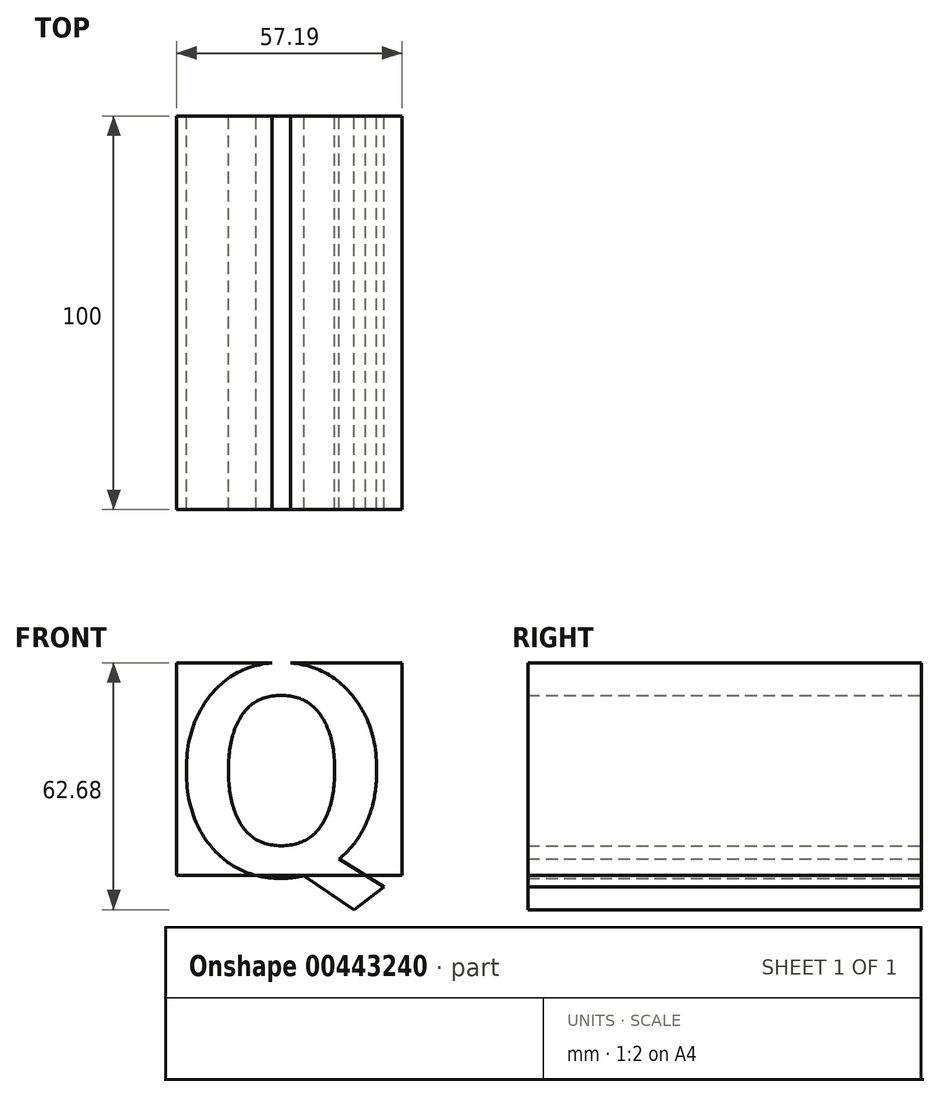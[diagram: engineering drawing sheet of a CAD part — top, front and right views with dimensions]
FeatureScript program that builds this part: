
annotation { "Feature Type Name" : "Feature", "Feature Type Description" : "" }
export const myFeature = defineFeature(function(context is Context, id is Id, definition is map)
    precondition{}
    {
        {
            var Q0;
            Q0=qCreatedBy(makeId("Front.planeOp"),FACE);
            var sketch = newSketch(context, id + "F0", { "sketchPlane" : qUnion([Q0])});
            skLineSegment(sketch, "E0.bottom", {"start": v(0, 0) * mm, "end": v(57.2, 0) * mm});
            skLineSegment(sketch, "E0.top", {"start": v(0, 53.97) * mm, "end": v(57.2, 53.97) * mm});
            skLineSegment(sketch, "E0.left", {"start": v(0, 0) * mm, "end": v(0, 53.97) * mm});
            skLineSegment(sketch, "E0.right", {"start": v(57.2, 0) * mm, "end": v(57.2, 53.97) * mm});
            skText(sketch, "E1", { "text": "Q", "fontName": "RobotoSlab-Bold.ttf"});
            const initialGuessF0  = {"E1": [0, 0, 1, 0, 0.05397]};
            skSetInitialGuess(sketch, initialGuessF0);
            skSolve(sketch);
        }
        {
            var Q0;
            {var subQ4=sQuery(id+"F0.wireOp",EDGE,"E0.left");Q0=makeQuery(id+"F0.imprint","IMPRINT",FACE,{"disambiguationData":[TD([[makeQuery(id+"F0.imprint","IMPRINT",EDGE,{"derivedFrom":subQ4}),-1.0]])]});}
            var Q1;
            Q1=makeQuery(id+"F0.imprint","IMPRINT",FACE,{"disambiguationData":[TD([[makeQuery(id+"F0.imprint","IMPRINT",EDGE,{"derivedFrom":sQuery(id+"F0.wireOp",EDGE,"E1.sketch_text.stroke-15")}),1.0]])]});
            var Q2;
            {var subQ0=sQuery(id+"F0.wireOp",EDGE,"E0.right");Q2=makeQuery(id+"F0.imprint","IMPRINT",FACE,{"disambiguationData":[TD([[makeQuery(id+"F0.imprint","IMPRINT",EDGE,{"derivedFrom":subQ0}),1.0]])]});}
            var Q3;
            {var subQ0=sQuery(id+"F0.wireOp",EDGE,"E1.sketch_text.stroke-3");Q3=makeQuery(id+"F0.imprint","IMPRINT",FACE,{"disambiguationData":[TD([[makeQuery(id+"F0.imprint","IMPRINT",EDGE,{"derivedFrom":subQ0}),-1.0]])]});}
            extrude(context, id + "F1", {"entities" : qUnion([Q0, Q1, Q2, Q3]), "depth" : 100 * mm});
        }
    });
